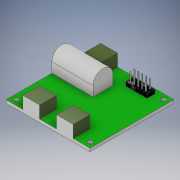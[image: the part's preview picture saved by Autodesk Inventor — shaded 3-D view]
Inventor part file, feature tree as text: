
AUTODESK INVENTOR PART (.ipt)
format: ipt  version: 2019 (Build 230136000, 136)  size: 288,768 bytes
history: native  units: mm
features: extrude x6, sketch x6, fillet x1
ambient origin geometry x8: Origin, YZ Plane, XZ Plane, XY Plane, X Axis, Y Axis, Z Axis, Center Point
bodies: Solid1 (feature_tree)
feature tree (13):
  extrude  "Extrusion1"  Depth=55.0mm
  extrude  "Extrusion2"  Depth=3.0mm
  extrude  "Extrusion3"  Depth=3.0mm
  extrude  "Extrusion4"  Depth=8.0mm
  fillet  "Fillet1"  Radius=5.0mm
  extrude  "Extrusion5"  Depth=5.0mm
  extrude  "Extrusion6"  Depth=5.0mm
  sketch  "Sketch1"  dims[d0=55.0mm d1=55.0mm]
  sketch  "Sketch2"  dims[d6=3.0mm d7=3.0mm]
  sketch  "Sketch3"  dims[d8=3.0mm d9=3.0mm]
  sketch  "Sketch4"  dims[d10=16.6mm d11=8.0mm d12=5.0mm]
  sketch  "Sketch5"  dims[d13=7.0mm d14=5.0mm]
  sketch  "Sketch6"  dims[d15=7.0mm d16=5.0mm d17=2.0mm d18=0.0mm d19=11.0mm d22=11.0mm d25=11.0mm d26=11.0mm d27=11.0mm d28=11.0mm d29=8.0mm d30=0.0mm d31=7.0mm d32=11.0mm d33=11.0mm d34=8.0mm d35=0.0mm d36=12.0mm d37=27.0mm d38=13.0mm d39=13.0mm d40=0.0mm d41=6.5mm d42=1.27mm d43=2.54mm d44=2.54mm d45=2.54mm d46=2.54mm d47=2.54mm d48=0.5mm d49=0.5mm d50=0.5mm d51=0.5mm d52=0.5mm d53=0.5mm d54=0.5mm d55=0.5mm d56=0.5mm d57=0.5mm d58=0.5mm d59=0.5mm d60=8.5mm d61=0.0mm d62=2.5mm d63=2.0mm d64=0.0mm d65=0.0mm]
